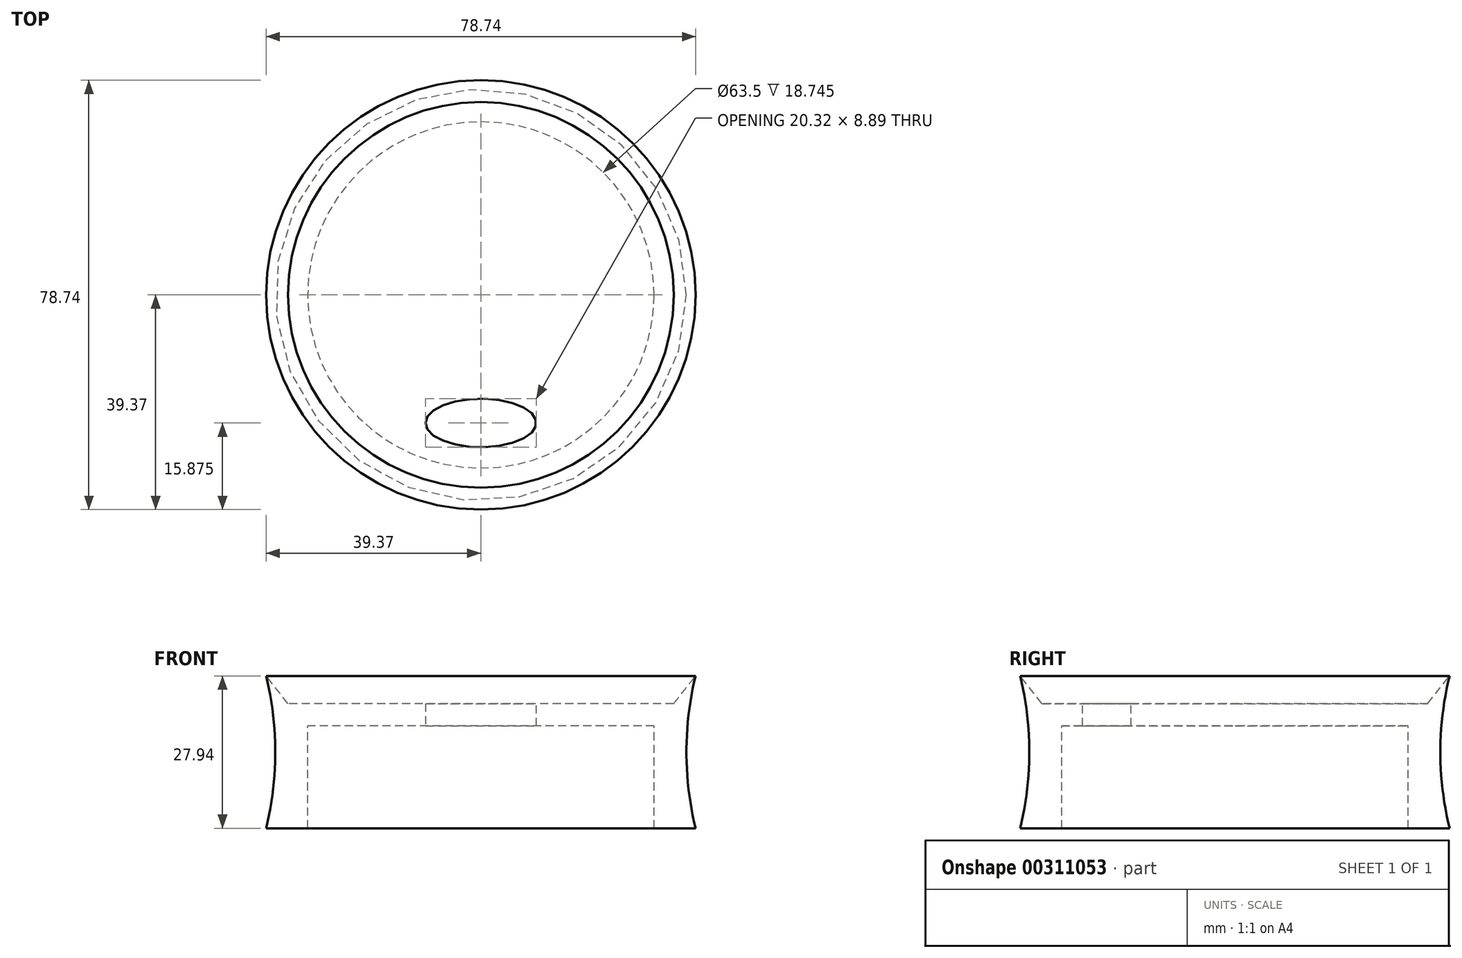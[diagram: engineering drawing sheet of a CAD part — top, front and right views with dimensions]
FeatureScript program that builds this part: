
annotation { "Feature Type Name" : "Feature", "Feature Type Description" : "" }
export const myFeature = defineFeature(function(context is Context, id is Id, definition is map)
    precondition{}
    {
        {
            var Q0;
            Q0=qCreatedBy(makeId("Front.planeOp"),FACE);
            var sketch = newSketch(context, id + "F0", { "sketchPlane" : qUnion([Q0])});
            skLineSegment(sketch, "E0", {"start": v(0, 0) * mm, "end": v(31.75, 0) * mm, "construction": true});
            skLineSegment(sketch, "E1", {"start": v(31.75, 0) * mm, "end": v(39.37, 0) * mm});
            skArc(sketch, "E2", {"start": v(39.37, 27.94) * mm, "mid": v(37.68, 13.97) * mm, "end": v(39.37, 0) * mm});
            skLineSegment(sketch, "E3", {"start": v(39.37, 27.94) * mm, "end": v(35.36, 22.86) * mm});
            skLineSegment(sketch, "E4", {"start": v(35.36, 22.86) * mm, "end": v(0, 22.86) * mm});
            skLineSegment(sketch, "E5", {"start": v(0, 22.86) * mm, "end": v(0, 18.75) * mm});
            skLineSegment(sketch, "E6", {"start": v(0, 18.75) * mm, "end": v(31.75, 18.75) * mm});
            skLineSegment(sketch, "E7", {"start": v(31.75, 18.75) * mm, "end": v(31.75, 0) * mm});
            skSolve(sketch);
        }
        {
            var Q0;
            Q0=makeQuery(id+"F0.imprint","IMPRINT",FACE,{"disambiguationData":[TD([[makeQuery(id+"F0.imprint","IMPRINT",EDGE,{"derivedFrom":sQuery(id+"F0.wireOp",EDGE,"E1")}),1.0]])]});
            var Q1;
            Q1=sQuery(id+"F0.wireOp",EDGE,"E5");
            revolve(context, id + "F1", {"entities" : qUnion([Q0]), "axis" : qUnion([Q1]), "revolveType" : RevolveType.FULL});
        }
        {
            var Q0;
            Q0=qCreatedBy(makeId("Top.planeOp"),FACE);
            var sketch = newSketch(context, id + "F2", { "sketchPlane" : qUnion([Q0])});
            skLineSegment(sketch, "E8", {"start": v(0, 0) * mm, "end": v(0, -23.5) * mm});
            skLineSegment(sketch, "E9", {"start": v(0, -23.5) * mm, "end": v(10.16, -23.5) * mm, "construction": true});
            skLineSegment(sketch, "E10", {"start": v(0, -23.5) * mm, "end": v(0, -19.05) * mm, "construction": true});
            skEllipse(sketch, "E11", {"center": v(0, -23.5) * mm, "majorRadius": 4.45 * mm, "minorRadius": 10.16 * mm, "majorAxis": v(0, 1)});
            skSolve(sketch);
        }
        {
            var Q0;
            Q0=makeQuery(id+"F2.imprint","IMPRINT",FACE,{"disambiguationData":[TD([[makeQuery(id+"F2.imprint","IMPRINT",EDGE,{"derivedFrom":sQuery(id+"F2.wireOp",EDGE,"E11")}),1.0]])]});
            var Q1;
            Q1=sQuery(id+"F2.wireOp",EDGE,"E11");
            extrude(context, id + "F3", {"entities" : qUnion([Q0]), "operationType" : NewBodyOperationType.REMOVE, "surfaceEntities" : qUnion([Q1]), "endBound" : BoundingType.THROUGH_ALL, "depth" : 46.48 * mm});
        }
    });
